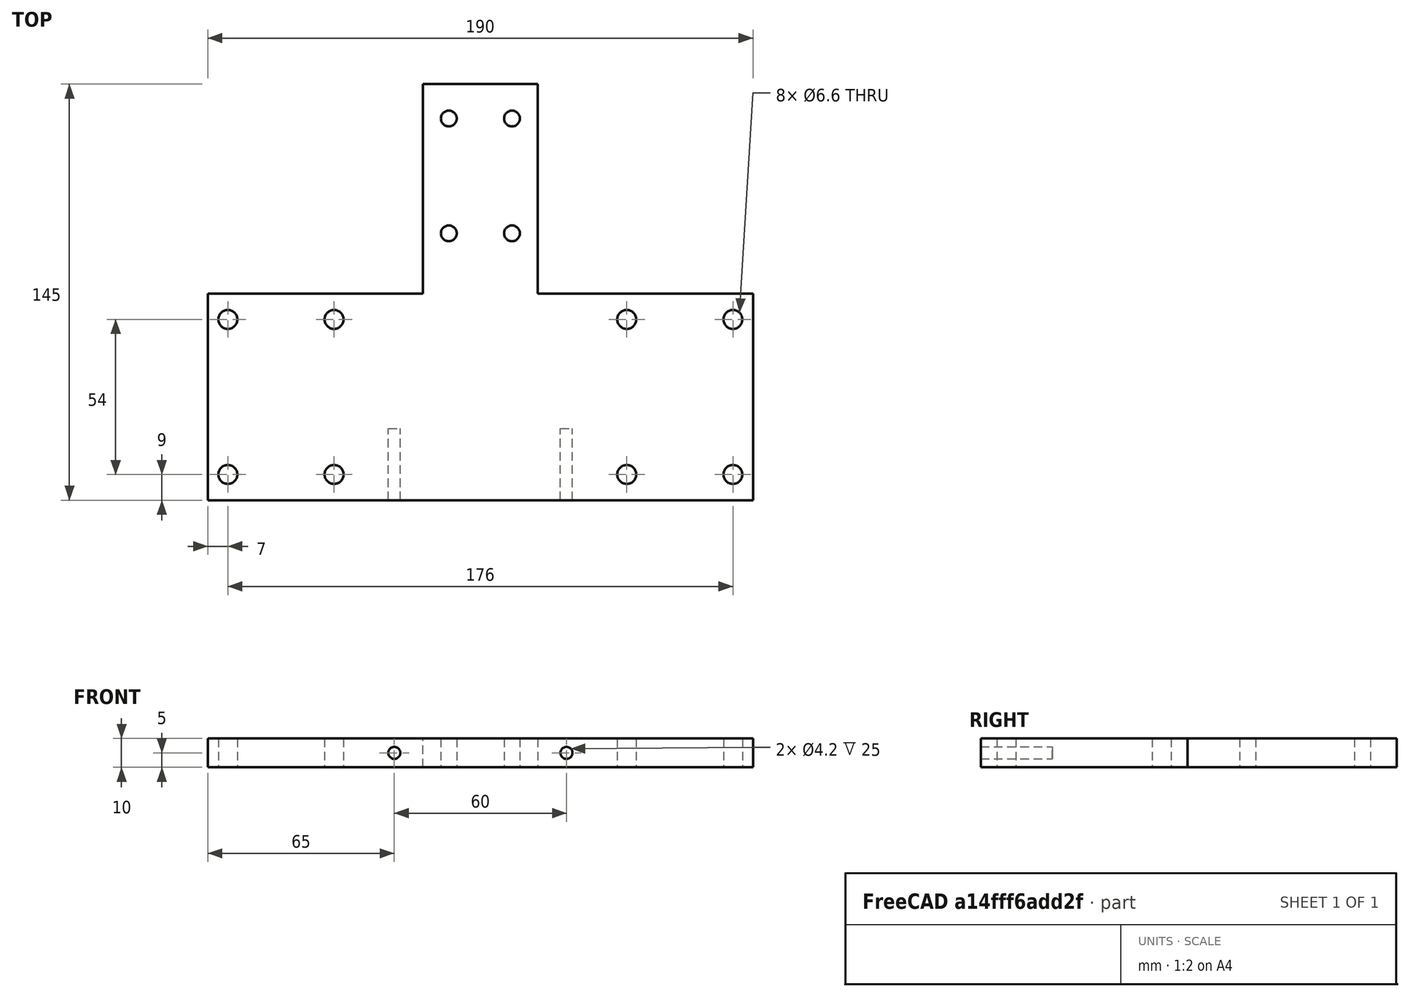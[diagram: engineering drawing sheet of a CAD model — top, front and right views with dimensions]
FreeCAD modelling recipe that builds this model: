
FCSTD DOCUMENT  (FreeCAD 0.17R13528 (Git))
Label: plate5
License: All rights reserved
LicenseURL: http://en.wikipedia.org/wiki/All_rights_reserved
objects: TechDraw::DrawViewDimension×29, PartDesign::LinearPattern×9, Sketcher::SketchObject×7, PartDesign::Hole×5, TechDraw::DrawProjGroupItem×3, PartDesign::Pad×2, PartDesign::Body×1, TechDraw::DrawSVGTemplate×1, TechDraw::DrawProjGroup×1, TechDraw::DrawViewAnnotation×1, TechDraw::DrawViewDetail×1, TechDraw::DrawPage×1
note: 31 computed .brp shape members not serialized (recipe doc carries the construction recipe); baked Part::Feature solids carry a one-line shape summary decoded from their .brp

FEATURE [Sketcher::SketchObject] Sketch
  MapMode = 5
  Support = -> [XY_Plane]
  sketch-geometry (4):
    g0: LineSegment StartX=0 StartY=0 StartZ=0 EndX=190 EndY=0 EndZ=0
    g1: LineSegment StartX=190 StartY=0 StartZ=0 EndX=190 EndY=72 EndZ=0
    g2: LineSegment StartX=190 StartY=72 StartZ=0 EndX=0 EndY=72 EndZ=0
    g3: LineSegment StartX=0 StartY=72 StartZ=0 EndX=0 EndY=0 EndZ=0
  constraints (11):
    c: Coincident(g0,g1)
    c: Coincident(g1,g2)
    c: Coincident(g2,g3)
    c: Coincident(g3,g0)
    c: Horizontal(g0)
    c: Horizontal(g2)
    c: Vertical(g1)
    c: Vertical(g3)
    c: Coincident(g0,g-1)
    c: DistanceX(g0,g0) = 190
    c: DistanceY(g3,g3) = 72
FEATURE [PartDesign::Pad] Pad
  Length = 10
  Length2 = 100
  Profile = -> Sketch
  Type = 0
FEATURE [Sketcher::SketchObject] Sketch001
  MapMode = 5
  Placement = pos=(0,72,0) rot=(0,0.707107,0.707107;3.14159rad)
  Support = -> [Pad]
  sketch-geometry (4):
    g0: LineSegment StartX=-115 StartY=0 StartZ=0 EndX=-75 EndY=0 EndZ=0
    g1: LineSegment StartX=-75 StartY=0 StartZ=0 EndX=-75 EndY=10 EndZ=0
    g2: LineSegment StartX=-75 StartY=10 StartZ=0 EndX=-115 EndY=10 EndZ=0
    g3: LineSegment StartX=-115 StartY=10 StartZ=0 EndX=-115 EndY=0 EndZ=0
  constraints (12):
    c: Coincident(g0,g1)
    c: Coincident(g1,g2)
    c: Coincident(g2,g3)
    c: Coincident(g3,g0)
    c: Horizontal(g0)
    c: Horizontal(g2)
    c: Vertical(g1)
    c: Vertical(g3)
    c: PointOnObject(g0,g-1)
    c: DistanceX(g2,g2) = 40
    c: DistanceY(g1,g1) = 10
    c: DistanceX(g0,g-1) = 75
FEATURE [PartDesign::Pad] Pad001
  BaseFeature = -> Pad
  Length = 73
  Length2 = 100
  Profile = -> Sketch001
  Type = 0
FEATURE [Sketcher::SketchObject] Sketch002
  MapMode = 5
  Placement = pos=(0,0,10) rot=(0,0,1;0rad)
  Support = -> [Pad001]
  sketch-geometry (1):
    g0: Circle CenterX=7 CenterY=9 CenterZ=0 NormalX=0 NormalY=0 NormalZ=1 AngleXU=0 Radius=6.05085
  constraints (2):
    c: Distance(g0,g-1) = 9
    c: Distance(g0,g-2) = 7
FEATURE [PartDesign::Hole] Hole
  BaseFeature = -> Pad001
  Depth = 25
  DepthType = 1
  Diameter = 6.6
  DrillPoint = 0
  DrillPointAngle = 118
  HoleCutCountersinkAngle = 90
  HoleCutDepth = 0
  HoleCutDiameter = 6
  HoleCutType = 0
  ModelActualThread = false
  Profile = -> Sketch002
  Tapered = false
  TaperedAngle = 90
  ThreadAngle = 0
  ThreadClass = 0
  ThreadCutOffInner = 0
  ThreadCutOffOuter = 0
  ThreadDirection = 0
  ThreadFit = 0
  ThreadPitch = 0
  ThreadSize = 7
  ThreadType = 1
  Threaded = false
FEATURE [PartDesign::LinearPattern] LinearPattern
  BaseFeature = -> Hole
  Direction = -> Sketch002 [H_Axis]
  Length = 37
  Occurrences = 2
  Originals = -> [Hole]
FEATURE [PartDesign::LinearPattern] LinearPattern001
  BaseFeature = -> LinearPattern
  Direction = -> Sketch002 [H_Axis]
  Length = 139
  Occurrences = 2
  Originals = -> [Hole]
FEATURE [PartDesign::LinearPattern] LinearPattern002
  BaseFeature = -> LinearPattern001
  Direction = -> Sketch002 [H_Axis]
  Length = 176
  Occurrences = 2
  Originals = -> [Hole]
FEATURE [Sketcher::SketchObject] Sketch003
  MapMode = 5
  Placement = pos=(0,0,10) rot=(0,0,1;0rad)
  Support = -> [LinearPattern002]
  sketch-geometry (1):
    g0: Circle CenterX=7 CenterY=63 CenterZ=0 NormalX=0 NormalY=0 NormalZ=1 AngleXU=0 Radius=6.81856
  constraints (2):
    c: Distance(g0,g-1) = 63
    c: Distance(g0,g-2) = 7
FEATURE [PartDesign::Hole] Hole001
  BaseFeature = -> LinearPattern002
  Depth = 25
  DepthType = 1
  Diameter = 6.6
  DrillPoint = 0
  DrillPointAngle = 118
  HoleCutCountersinkAngle = 90
  HoleCutDepth = 0
  HoleCutDiameter = 6
  HoleCutType = 0
  ModelActualThread = false
  Profile = -> Sketch003
  Tapered = false
  TaperedAngle = 90
  ThreadAngle = 0
  ThreadClass = 0
  ThreadCutOffInner = 0
  ThreadCutOffOuter = 0
  ThreadDirection = 0
  ThreadFit = 0
  ThreadPitch = 0
  ThreadSize = 7
  ThreadType = 1
  Threaded = false
FEATURE [PartDesign::LinearPattern] LinearPattern003
  BaseFeature = -> Hole001
  Direction = -> Sketch003 [H_Axis]
  Length = 37
  Occurrences = 2
  Originals = -> [Hole001]
FEATURE [PartDesign::LinearPattern] LinearPattern004
  BaseFeature = -> LinearPattern003
  Direction = -> Sketch003 [H_Axis]
  Length = 139
  Occurrences = 2
  Originals = -> [Hole001]
FEATURE [PartDesign::LinearPattern] LinearPattern005
  BaseFeature = -> LinearPattern004
  Direction = -> Sketch003 [H_Axis]
  Length = 176
  Occurrences = 2
  Originals = -> [Hole001]
FEATURE [Sketcher::SketchObject] Sketch004
  MapMode = 5
  Placement = pos=(0,0,10) rot=(0,0,1;0rad)
  Support = -> [LinearPattern005]
  sketch-geometry (1):
    g0: Circle CenterX=84 CenterY=93 CenterZ=0 NormalX=0 NormalY=0 NormalZ=1 AngleXU=0 Radius=4.83652
  constraints (2):
    c: Distance(g0,g-1) = 93
    c: Distance(g0,g-2) = 84
FEATURE [PartDesign::Hole] Hole002
  BaseFeature = -> LinearPattern005
  Depth = 25
  DepthType = 1
  Diameter = 5.5
  DrillPoint = 0
  DrillPointAngle = 118
  HoleCutCountersinkAngle = 90
  HoleCutDepth = 0
  HoleCutDiameter = 5
  HoleCutType = 0
  ModelActualThread = false
  Profile = -> Sketch004
  Tapered = false
  TaperedAngle = 90
  ThreadAngle = 0
  ThreadClass = 0
  ThreadCutOffInner = 0
  ThreadCutOffOuter = 0
  ThreadDirection = 0
  ThreadFit = 0
  ThreadPitch = 0
  ThreadSize = 6
  ThreadType = 1
  Threaded = false
FEATURE [PartDesign::LinearPattern] LinearPattern006
  BaseFeature = -> Hole002
  Direction = -> Sketch004 [H_Axis]
  Length = 22
  Occurrences = 2
  Originals = -> [Hole002]
FEATURE [PartDesign::LinearPattern] LinearPattern007
  BaseFeature = -> LinearPattern006
  Direction = -> Sketch004 [V_Axis]
  Length = 40
  Occurrences = 2
  Originals = -> [Hole002]
FEATURE [Sketcher::SketchObject] Sketch005
  MapMode = 5
  Placement = pos=(0,0,10) rot=(0,0,1;0rad)
  Support = -> [LinearPattern007]
  sketch-geometry (1):
    g0: Circle CenterX=106 CenterY=133 CenterZ=0 NormalX=0 NormalY=0 NormalZ=1 AngleXU=0 Radius=4.41768
  constraints (2):
    c: Distance(g0,g-1) = 133
    c: Distance(g0,g-2) = 106
FEATURE [PartDesign::Hole] Hole003
  BaseFeature = -> LinearPattern007
  Depth = 25
  DepthType = 1
  Diameter = 5.5
  DrillPoint = 0
  DrillPointAngle = 118
  HoleCutCountersinkAngle = 90
  HoleCutDepth = 0
  HoleCutDiameter = 5
  HoleCutType = 0
  ModelActualThread = false
  Profile = -> Sketch005
  Tapered = false
  TaperedAngle = 90
  ThreadAngle = 0
  ThreadClass = 0
  ThreadCutOffInner = 0
  ThreadCutOffOuter = 0
  ThreadDirection = 0
  ThreadFit = 0
  ThreadPitch = 0
  ThreadSize = 6
  ThreadType = 1
  Threaded = false
FEATURE [Sketcher::SketchObject] Sketch006
  MapMode = 5
  Placement = pos=(0,0,0) rot=(1,0,0;1.5708rad)
  Support = -> [Hole003]
  sketch-geometry (1):
    g0: Circle CenterX=65 CenterY=5 CenterZ=0 NormalX=0 NormalY=0 NormalZ=1 AngleXU=0 Radius=5.10504
  constraints (2):
    c: Distance(g0,g-1) = 5
    c: Distance(g0,g-2) = 65
FEATURE [PartDesign::Hole] Hole004
  BaseFeature = -> Hole003
  Depth = 25
  DepthType = 0
  Diameter = 4.2
  DrillPoint = 0
  DrillPointAngle = 118
  HoleCutCountersinkAngle = 90
  HoleCutDepth = 0
  HoleCutDiameter = 5
  HoleCutType = 0
  ModelActualThread = false
  Profile = -> Sketch006
  Tapered = false
  TaperedAngle = 90
  ThreadAngle = 60
  ThreadClass = 0
  ThreadCutOffInner = 0.0866025
  ThreadCutOffOuter = 0.173205
  ThreadDirection = 1
  ThreadFit = 0
  ThreadPitch = 0.8
  ThreadSize = 6
  ThreadType = 1
  Threaded = true
FEATURE [PartDesign::LinearPattern] LinearPattern008
  BaseFeature = -> Hole004
  Direction = -> Sketch006 [H_Axis]
  Length = 60
  Occurrences = 2
  Originals = -> [Hole004]
FEATURE [PartDesign::Body] Body
  Group = -> [Sketch,Pad,Sketch001,Pad001,Sketch002,Hole,LinearPattern,LinearPattern001,LinearPattern002,Sketch003,Hole001,LinearPattern003,LinearPattern004,LinearPattern005,Sketch004,Hole002,LinearPattern006,LinearPattern007,Sketch005,Hole003,Sketch006,Hole004,LinearPattern008]
  Origin = -> Origin
  Tip = -> LinearPattern008
FEATURE [TechDraw::DrawSVGTemplate] Template001
  EditableTexts = Designed_by_Name=Lukas Winter; FC-Date=02.08.2018; FC-SC=1:2; FC-SH=1/1; FC-Title=COSI Measure v1.0; Subtitle=Mechanical assembly - plate 5
  Height = 210
  Orientation = 1
  Width = 297
FEATURE [TechDraw::DrawProjGroupItem] ProjItem  label="Front"
  CoarseView = false
  Direction = (0,-1,0)
  Focus = 100
  HardHidden = false
  IsoCount = 0
  IsoHidden = false
  IsoVisible = false
  LockPosition = false
  Perspective = false
  Rotation = 0
  RotationVector = (1,0,0)
  ScaleType = 0
  SeamHidden = false
  SeamVisible = false
  SmoothHidden = false
  SmoothVisible = false
  Source = -> [Body]
  Type = 0
  X = 81.25
  Y = 93.8946
FEATURE [TechDraw::DrawProjGroupItem] ProjItem001  label="Right"
  CoarseView = false
  Direction = (1,0,0)
  Focus = 100
  HardHidden = false
  IsoCount = 0
  IsoHidden = false
  IsoVisible = false
  LockPosition = false
  Perspective = false
  Rotation = 0
  RotationVector = (0,-1,0)
  Scale = 0.5
  ScaleType = 2
  SeamHidden = false
  SeamVisible = false
  SmoothHidden = false
  SmoothVisible = false
  Source = -> [Body]
  Type = 2
  X = 110
  Y = 0
FEATURE [TechDraw::DrawProjGroupItem] ProjItem002  label="Bottom"
  CoarseView = false
  Direction = (0,0,-1)
  Focus = 100
  HardHidden = false
  IsoCount = 0
  IsoHidden = false
  IsoVisible = false
  LockPosition = false
  Perspective = false
  Rotation = 0
  RotationVector = (1,0,0)
  Scale = 0.5
  ScaleType = 2
  SeamHidden = false
  SeamVisible = false
  SmoothHidden = false
  SmoothVisible = false
  Source = -> [Body]
  Type = 5
  X = 0
  Y = -87.5
FEATURE [TechDraw::DrawProjGroup] ProjGroup
  Anchor = -> ProjItem
  AutoDistribute = true
  CubeDirs = (6) [(0,2.44929e-16,-1),(0,-1,-2.44929e-16),(-1,0,0),(0,1,2.44929e-16),(1,0,0),(0,-2.44929e-16,1)]
  CubeRotations = (6) [(1,0,0),(1,0,0),(0,1,-2.44929e-16),(-1,0,0),(0,-1,2.44929e-16),(1,0,0)]
  LockPosition = false
  ProjectionType = 2
  Rotation = 0
  Scale = 0.5
  ScaleType = 2
  Source = -> [Body]
  Views = -> [ProjItem,ProjItem001,ProjItem002]
  X = 83.144
  Y = 164.706
  spacingX = 15
  spacingY = 15
FEATURE [TechDraw::DrawViewDimension] Dimension
  FormatSpec = %.2f
  LockPosition = false
  MeasureType = 1
  References2D = -> [ProjItem001]
  Rotation = 0
  ScaleType = 0
  Type = 2
  X = 49.7778
  Y = -13.7407
FEATURE [TechDraw::DrawViewDimension] Dimension001
  FormatSpec = %.2f
  LockPosition = false
  MeasureType = 1
  References2D = -> [ProjItem002]
  Rotation = 0
  ScaleType = 0
  Type = 2
  X = -62.7407
  Y = 11.9259
FEATURE [TechDraw::DrawViewDimension] Dimension002
  FormatSpec = %.2f
  LockPosition = false
  MeasureType = 1
  References2D = -> [ProjItem002]
  Rotation = 0
  ScaleType = 0
  Type = 2
  X = -62.7407
  Y = -17.6296
FEATURE [TechDraw::DrawViewDimension] Dimension003
  FormatSpec = %.2f
  LockPosition = false
  MeasureType = 1
  References2D = -> [ProjItem002]
  Rotation = 0
  ScaleType = 0
  Type = 5
  X = 31.0104
  Y = -17.9208
FEATURE [TechDraw::DrawViewDimension] Dimension006
  FormatSpec = %.2f
  LockPosition = false
  MeasureType = 1
  References2D = -> [ProjItem002]
  Rotation = 0
  ScaleType = 0
  Type = 5
  X = 38.0146
  Y = -35.6473
FEATURE [TechDraw::DrawViewDimension] Dimension007
  FormatSpec = %.2f
  LockPosition = false
  MeasureType = 1
  References2D = -> [ProjItem002]
  Rotation = 0
  ScaleType = 0
  Type = 5
  X = 73.6368
  Y = 25.9259
FEATURE [TechDraw::DrawViewDimension] Dimension008
  FormatSpec = %.2f
  LockPosition = false
  MeasureType = 1
  References2D = -> [ProjItem002]
  Rotation = 0
  ScaleType = 0
  Type = 5
  X = 73.8169
  Y = -1.62037
FEATURE [TechDraw::DrawViewDimension] Dimension009
  FormatSpec = %.2f
  LockPosition = false
  MeasureType = 1
  References2D = -> [ProjItem002]
  Rotation = 0
  ScaleType = 0
  Type = 2
  X = 28.3678
  Y = 21.8891
FEATURE [TechDraw::DrawViewDimension] Dimension010
  FormatSpec = %.2f
  LockPosition = false
  MeasureType = 1
  References2D = -> [ProjItem002]
  Rotation = 0
  ScaleType = 0
  Type = 1
  X = 35.5257
  Y = 58.8519
FEATURE [TechDraw::DrawViewDimension] Dimension011
  FormatSpec = %.2f
  LockPosition = false
  MeasureType = 1
  References2D = -> [ProjItem002]
  Rotation = 0
  ScaleType = 0
  Type = 1
  X = 55.7912
  Y = 46.6595
FEATURE [TechDraw::DrawViewDimension] Dimension012
  FormatSpec = %.2f
  LockPosition = false
  MeasureType = 1
  References2D = -> [ProjItem002]
  Rotation = 0
  ScaleType = 0
  Type = 2
  X = 17.8241
  Y = 18.0041
FEATURE [TechDraw::DrawViewDimension] Dimension013
  FormatSpec = %.2f
  LockPosition = false
  MeasureType = 1
  References2D = -> [ProjItem002]
  Rotation = 0
  ScaleType = 0
  Type = 1
  X = 4.14095
  Y = 59.0535
FEATURE [TechDraw::DrawViewDimension] Dimension014
  FormatSpec = %.2f
  LockPosition = false
  MeasureType = 1
  References2D = -> [ProjItem002]
  Rotation = 0
  ScaleType = 0
  Type = 1
  X = -33.963
  Y = 59.1111
FEATURE [TechDraw::DrawViewDimension] Dimension015
  FormatSpec = %.2f
  LockPosition = false
  MeasureType = 1
  References2D = -> [ProjItem002]
  Rotation = 0
  ScaleType = 0
  Type = 1
  X = -56.2593
  Y = 49.2593
FEATURE [TechDraw::DrawViewDimension] Dimension016
  FormatSpec = %.2f
  LockPosition = false
  MeasureType = 1
  References2D = -> [ProjItem002]
  Rotation = 0
  ScaleType = 0
  Type = 1
  X = 2.59259
  Y = -19.4444
FEATURE [TechDraw::DrawViewDimension] Dimension017
  FormatSpec = %.2f
  LockPosition = false
  MeasureType = 1
  References2D = -> [ProjItem002]
  Rotation = 0
  ScaleType = 0
  Type = 1
  X = -19.1333
  Y = -49
FEATURE [TechDraw::DrawViewDimension] Dimension018
  FormatSpec = %.2f
  LockPosition = false
  MeasureType = 1
  References2D = -> [ProjItem002]
  Rotation = 0
  ScaleType = 0
  Type = 1
  X = 22.5556
  Y = -2.59259
FEATURE [TechDraw::DrawViewDimension] Dimension019
  FormatSpec = %.2f
  LockPosition = false
  MeasureType = 1
  References2D = -> [ProjItem002]
  Rotation = 0
  ScaleType = 0
  Type = 2
  X = -23.8519
  Y = -19.7037
FEATURE [TechDraw::DrawViewDimension] Dimension020
  FormatSpec = %.2f
  LockPosition = false
  MeasureType = 1
  References2D = -> [ProjItem002]
  Rotation = 0
  ScaleType = 0
  Type = 2
  X = -33.0988
  Y = -33.7901
FEATURE [TechDraw::DrawViewDimension] Dimension021
  FormatSpec = %.2f
  LockPosition = false
  MeasureType = 1
  References2D = -> [ProjItem002]
  Rotation = 0
  ScaleType = 0
  Type = 2
  X = -36.4
  Y = -0.933334
FEATURE [TechDraw::DrawViewDimension] Dimension022
  FormatSpec = %.2f
  LockPosition = false
  MeasureType = 1
  References2D = -> [ProjItem]
  Rotation = 0
  ScaleType = 0
  Type = 1
  X = 1.24444
  Y = 18.9778
FEATURE [TechDraw::DrawViewDimension] Dimension023
  FormatSpec = %.2f
  LockPosition = false
  MeasureType = 1
  References2D = -> [ProjItem]
  Rotation = 0
  ScaleType = 0
  Type = 2
  X = 21.1556
  Y = -12.7556
FEATURE [TechDraw::DrawViewDimension] Dimension024
  FormatSpec = %.2f
  LockPosition = false
  MeasureType = 1
  References2D = -> [ProjItem]
  Rotation = 0
  ScaleType = 0
  Type = 1
  X = 30.1778
  Y = 18.9778
FEATURE [TechDraw::DrawViewAnnotation] Annotation
  Font = osifont
  LineSpace = 80
  LockPosition = false
  MaxWidth = -1
  Rotation = 0
  ScaleType = 0
  Text = Threaded M5x20mm
  TextSize = 4
  TextStyle = 0
  X = 213.833
  Y = 112.467
FEATURE [TechDraw::DrawViewDetail] Detail  label="Detail 1"
  AnchorPoint = (30,0,0)
  BaseView = -> ProjItem
  CoarseView = false
  Direction = (0,-1,0)
  Focus = 100
  HardHidden = false
  IsoCount = 0
  IsoHidden = false
  IsoVisible = false
  LockPosition = false
  Perspective = false
  Radius = 10
  Reference = 1
  Rotation = 0
  ScaleType = 0
  SeamHidden = false
  SeamVisible = false
  SmoothHidden = false
  SmoothVisible = false
  Source = -> [Body]
  X = 213.211
  Y = 95.0444
FEATURE [TechDraw::DrawViewDimension] Dimension025
  FormatSpec = %.2f
  LockPosition = false
  MeasureType = 1
  References2D = -> [ProjItem]
  Rotation = 0
  ScaleType = 0
  Type = 1
  X = 0
  Y = 28.687
FEATURE [TechDraw::DrawViewDimension] Dimension026
  FormatSpec = %.2f
  LockPosition = false
  MeasureType = 1
  References2D = -> [ProjItem001]
  Rotation = 0
  ScaleType = 0
  Type = 1
  X = -17.2679
  Y = 28.4085
FEATURE [TechDraw::DrawViewDimension] Dimension027
  FormatSpec = %.2f
  LockPosition = false
  MeasureType = 1
  References2D = -> [ProjItem001]
  Rotation = 0
  ScaleType = 0
  Type = 1
  X = 22.0027
  Y = 28.13
FEATURE [TechDraw::DrawViewDimension] Dimension028
  FormatSpec = %.2f
  LockPosition = false
  MeasureType = 1
  References2D = -> [ProjItem002]
  Rotation = 0
  ScaleType = 0
  Type = 1
  X = -25.9019
  Y = 18.939
FEATURE [TechDraw::DrawViewDimension] Dimension029
  FormatSpec = %.2f
  LockPosition = false
  MeasureType = 1
  References2D = -> [ProjItem002]
  Rotation = 0
  ScaleType = 0
  Type = 2
  X = -16.6513
  Y = 8.27979
FEATURE [TechDraw::DrawViewDimension] Dimension030
  FormatSpec = %.2f
  LockPosition = false
  MeasureType = 1
  References2D = -> [ProjItem002]
  Rotation = 0
  ScaleType = 0
  Type = 1
  X = 26.5741
  Y = -55.7407
FEATURE [TechDraw::DrawPage] Page001
  KeepUpdated = true
  ProjectionType = 0
  Template = -> Template001
  Views = -> [ProjGroup,Dimension,Dimension001,Dimension002,Dimension003,Dimension006,Dimension007,Dimension008,Dimension009,Dimension010,Dimension011,Dimension012,Dimension013,Dimension014,Dimension015,Dimension016,Dimension017,Dimension018,Dimension019,Dimension020,Dimension021,Dimension022,Dimension023,Dimension024,Annotation,Detail,Dimension025,Dimension026,Dimension027,Dimension028,Dimension029,+1 more]
